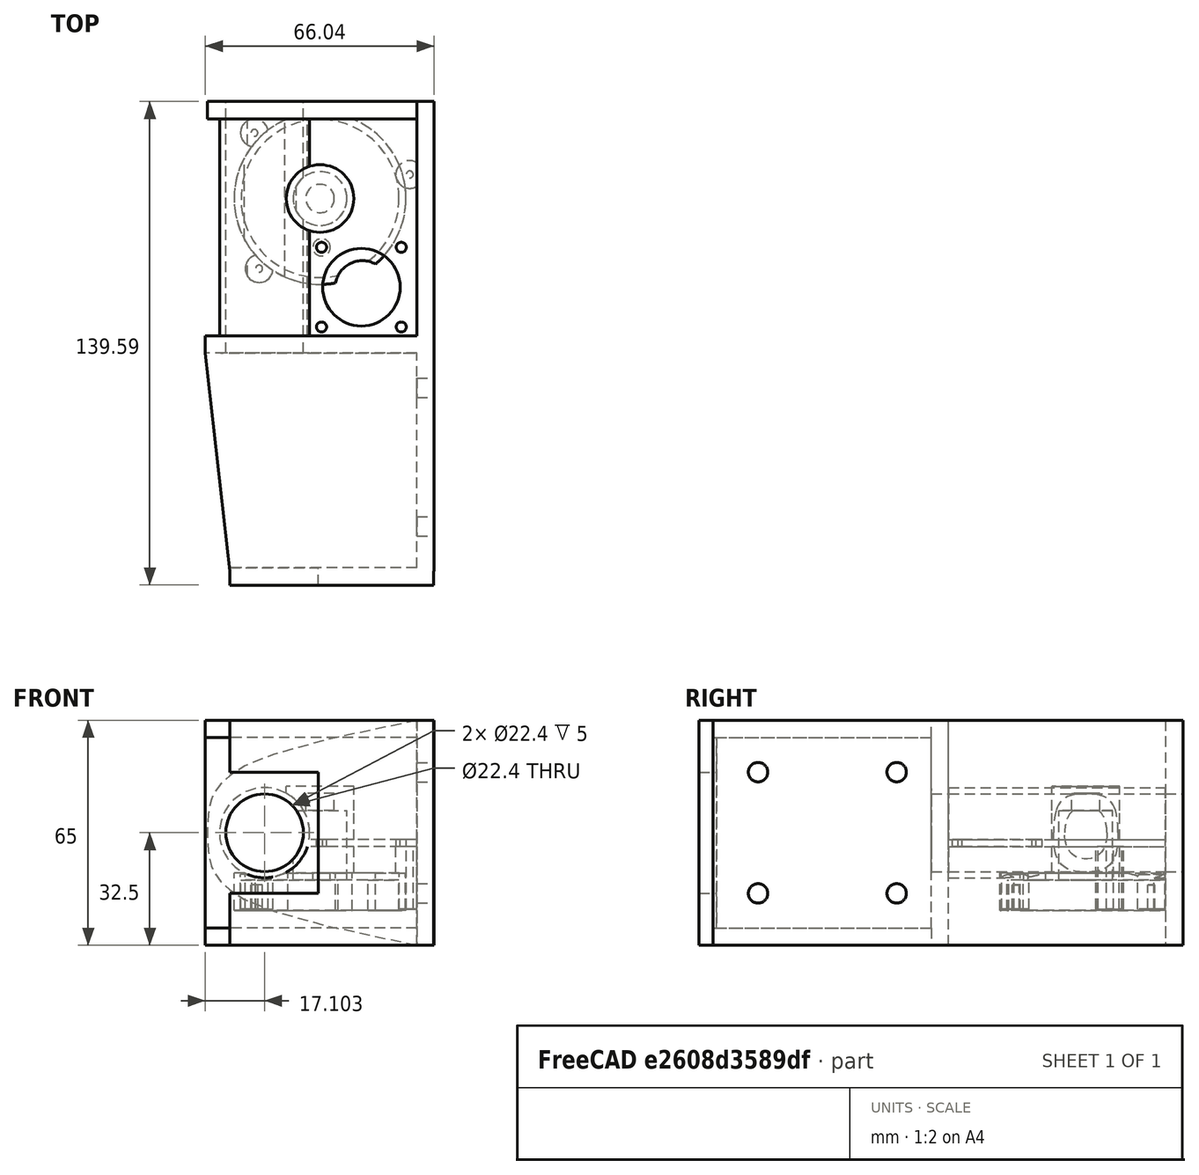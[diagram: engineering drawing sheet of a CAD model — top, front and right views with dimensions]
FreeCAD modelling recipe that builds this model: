
FCSTD DOCUMENT  (FreeCAD 0.18R16110 (Git))
Label: Thumb_Casing
License: All rights reserved
LicenseURL: http://en.wikipedia.org/wiki/All_rights_reserved
objects: Part::Cylinder×31, Part::Cut×27, Part::MultiFuse×6, Part::Box×6, Part::Wedge×2, Spreadsheet::Sheet×1, Sketcher::SketchObject×1, Part::Extrusion×1, Mesh::Feature×1
note: 74 computed .brp shape members not serialized (recipe doc carries the construction recipe); baked Part::Feature solids carry a one-line shape summary decoded from their .brp

FEATURE [Part::Cylinder] Cylinder003  label="Zylinder003"
  Angle = 360
  AttacherType = Attacher::AttachEngine3D
  Height = 72.5941
  Radius = 13
  expr: Height = Spreadsheet.z_l
  expr: Radius = Spreadsheet.z_ra + Spreadsheet.casing_srack
FEATURE [Part::Cylinder] Cylinder008  label="Zylinder008"
  Angle = 360
  AttacherType = Attacher::AttachEngine3D
  Height = 28.4
  Radius = 7.76
  expr: Height = Spreadsheet.z1_height + Spreadsheet.tolerance * 2
  expr: Radius = Spreadsheet.z1_da / 2 + Spreadsheet.tolerance * 2
FEATURE [Part::Cylinder] Cylinder004  label="Zylinder004"
  Angle = 360
  AttacherType = Attacher::AttachEngine3D
  Height = 72.5941
  Radius = 11.2
  expr: Height = Spreadsheet.z_l
  expr: Radius = Spreadsheet.z_ra + Spreadsheet.tolerance
FEATURE [Part::Cylinder] Cylinder007  label="Zylinder007"
  Angle = 360
  AttacherType = Attacher::AttachEngine3D
  Height = 8.8
  Placement = pos=(0,0,-0.4) rot=(0,0,1;0rad)
  Radius = 22.8
  expr: Placement.Base.z = -Spreadsheet.tolerance * 2
  expr: Height = Spreadsheet.z2_h + Spreadsheet.tolerance * 4
  expr: Radius = Spreadsheet.z2_da / 2 + Spreadsheet.tolerance * 2
FEATURE [Part::Cylinder] Cylinder010  label="Zylinder010"
  Angle = 360
  AttacherType = Attacher::AttachEngine3D
  Height = 5
  Radius = 4.1
FEATURE [Part::Cylinder] Cylinder006  label="Zylinder006"
  Angle = 360
  AttacherType = Attacher::AttachEngine3D
  Height = 28.4
  Radius = 9.76
  expr: Height = Spreadsheet.z1_height + Spreadsheet.tolerance * 2
  expr: Radius = Spreadsheet.z1_da / 2 + Spreadsheet.tolerance * 2 + Spreadsheet.casing_sgear
FEATURE [Part::Cylinder] Cylinder011  label="Zylinder011"
  Angle = 360
  AttacherType = Attacher::AttachEngine3D
  Height = 7
  Radius = 9.76
  expr: Height = Spreadsheet.casing_sgear + 5
  expr: Radius = Spreadsheet.z1_da / 2 + Spreadsheet.tolerance * 2 + Spreadsheet.casing_sgear
FEATURE [Part::Cylinder] Cylinder014  label="Zylinder014"
  Angle = 360
  AttacherType = Attacher::AttachEngine3D
  Height = 72.5941
  Placement = pos=(-9.44695,-21.4,12) rot=(-1,0,0;1.5708rad)
  Radius = 11.2
  expr: Placement.Base.z = Spreadsheet.z_h / 2
  expr: Height = Spreadsheet.z_l
  expr: Placement.Base.y = -(Spreadsheet.z2_da / 2 + Spreadsheet.casing_scase + Spreadsheet.casing_sgear - Spreadsheet.z1_yshift)
  expr: Placement.Base.x = -(Spreadsheet.z_ra * cos(asin(Spreadsheet.z_w / 2 / Spreadsheet.z_ra)) - Spreadsheet.modul)
  expr: Radius = Spreadsheet.z_ra + Spreadsheet.tolerance
FEATURE [Part::Cylinder] Cylinder015  label="Zylinder015"
  Angle = 360
  AttacherType = Attacher::AttachEngine3D
  Height = 10.8
  Placement = pos=(18.7793,-17.7754,-10.4) rot=(0,0,1;0rad)
  Radius = 7.84
  expr: Placement.Base.z = Spreadsheet.z2_zpos - Spreadsheet.tolerance * 2
  expr: Height = Spreadsheet.z2_h + 4 * Spreadsheet.tolerance + Spreadsheet.casing_sgear
  expr: Placement.Base.y = Spreadsheet.z1_yshift + sin(Spreadsheet.ritzel_angle) * (Spreadsheet.tolerance + Spreadsheet.z2_dc + Spreadsheet.ritzel_dc)
  expr: Placement.Base.x = Spreadsheet.z1_dc + Spreadsheet.tolerance + cos(Spreadsheet.ritzel_angle) * (Spreadsheet.tolerance + Spreadsheet.z2_dc + Spreadsheet.ritzel_dc)
  expr: Radius = Spreadsheet.ritzel_da / 2 + Spreadsheet.tolerance * 2
FEATURE [Part::Cylinder] Cylinder005  label="Zylinder005"
  Angle = 360
  AttacherType = Attacher::AttachEngine3D
  Height = 10.8
  Placement = pos=(0,0,-0.4) rot=(0,0,1;0rad)
  Radius = 24.8
  expr: Placement.Base.z = -Spreadsheet.tolerance * 2
  expr: Height = Spreadsheet.z2_h + 4 * Spreadsheet.tolerance + Spreadsheet.casing_sgear
  expr: Radius = Spreadsheet.z2_da / 2 + Spreadsheet.tolerance * 2 + Spreadsheet.casing_sgear
FEATURE [Part::MultiFuse] Fusion001
  Shapes = -> [Cylinder005,Cylinder006]
FEATURE [Part::Cylinder] Cylinder013  label="Zylinder013"
  Angle = 360
  AttacherType = Attacher::AttachEngine3D
  Height = 32.4
  Placement = pos=(6.76,8,-10.2) rot=(0,0,1;0rad)
  Radius = 9.56
  expr: Radius = Spreadsheet.z1_da / 2 + Spreadsheet.tolerance + Spreadsheet.casing_sgear
  expr: Placement.Base.y = Spreadsheet.z1_yshift
  expr: Placement.Base.x = Spreadsheet.z1_dc + Spreadsheet.tolerance
  expr: Placement.Base.z = -(Spreadsheet.z2_dr + Spreadsheet.z2_h - (Spreadsheet.z_h / 2 - Spreadsheet.z_ra) + Spreadsheet.tolerance)
  expr: Height = Spreadsheet.z_w / 2 + Spreadsheet.z2_dr + Spreadsheet.z2_h + Spreadsheet.z_ra + 2 * Spreadsheet.tolerance + Spreadsheet.casing_sgear + 4
FEATURE [Spreadsheet::Sheet] Spreadsheet
  cells = A1=Modul; B1(modul)=0.8; D1=tolerance; E1(tolerance)=0.2; G1=tolerance gear; H1(tolerance_gear)=0; A3=Zahnstange; D3=Zahnrad_1; G3=Zahnrad_2; J3=Ritzel; M3=Stepper; P3=Casing; A4=ra; B4(z_ra)=11; D4=#teeth; E4(z1_teeth)=16; G4=#teeth; H4(z2_teeth)=54; J4=#teeth; K4(ritzel_teeth)=16; M4=axis d; N4(stepper_daxis)=5; P4=gear casing sgear; Q4(casing_sgear)=2; A5=di; B5(z_ri)=8; D5=shift; E5(z1_shift)=0.2; G5=shift; H5(z2_shift)=0; J5=shift; K5(ritzel_shift)=0.3; M5=shaft l; N5(stepper_lshaft)=18; P5=rack casing srack; Q5(casing_srack)=2; A6=l; B6(z_l)==casing_ymax - casing_ymin + casing_scase; D6=pitch d; E6(z1_dpi)==modul * z1_teeth; G6=pitch d; H6(z2_dpi)==modul * z2_teeth; J6=pitch d; K6(ritzel_dpi)==modul * ritzel_teeth; M6=outside  sa; N6(stepper_sa)=28; P6=casing scase; Q6(casing_scase)=5; D7=outside d; E7(z1_da)==z1_dpi + 2 * (1 + z1_shift) * modul; G7=outside d; H7(z2_da)==z2_dpi + 2 * (1 + z2_shift) * modul; J7=outside d; K7(ritzel_da)==ritzel_dpi + 2 * (1 + ritzel_shift) * modul; M7=mount screw s; N7(stepper_sscrew)=23; P7=casing ssup; Q7(casing_ssup)=5; A8=rack height; B8(z_h)==z_th; D8=center distance; E8(z1_dc)==z1_dpi / 2 + z1_shift * modul + tolerance_gear; G8=center distance; H8(z2_dc)==z2_dpi / 2 + z2_shift * modul + tolerance_gear; J8=center distace; K8(ritzel_dc)==ritzel_dpi / 2 + ritzel_shift * modul + tolerance_gear; M8=mount d; N8(stepper_dmount)=22; P8=überlappung sjoin; Q8(casing_sjoin)=0.9; A9=rack thickness; B9(z_th)==2 * z_ra + 2; M9=mount heigth; N9(stepper_hmount)=2; A10=rack teeth width; B10(z_w)=8; D10=y Shift; E10(z1_yshift)=8; G10=height; H10(z2_h)=8; J10=angle z1; K10(ritzel_angle)=-65; M10=mount dscrew; N10(stepper_dscrew)=2.5; P10=casing y_min; Q10(casing_ymin)==-(Spreadsheet.z2_da / 2 + Spreadsheet.casing_scase + Spreadsheet.casing_sgear - Spreadsheet.z1_yshift - casing_sjoin + Spreadsheet.tolerance) * 0 + Spreadsheet.ritzel_ypos - stepper_sa / 2 - casing_scase; A11=#teeth; B11(z_teeth)=45; D11=height; E11(z1_height)==Spreadsheet.z_w * 3 / 4 + Spreadsheet.z2_dr + Spreadsheet.z2_h + Spreadsheet.z_ra; G11=distance rack; H11(z2_dr)=3; P11=casing x_min; Q11(casing_xmin)==-(Spreadsheet.z_ra * cos(asin(Spreadsheet.z_w / 2 / Spreadsheet.z_ra)) - Spreadsheet.modul + Spreadsheet.z_ra + Spreadsheet.casing_srack + Spreadsheet.casing_scase - Spreadsheet.casing_sjoin); D12=axis r; E12(z1_daxis)=2.5; G12=axis r; J12=x_pos; K12(ritzel_xpos)==Spreadsheet.z1_dc + cos(Spreadsheet.ritzel_angle) * (Spreadsheet.z2_dc + Spreadsheet.ritzel_dc); P12=casing z_min; Q12(casing_zmin)==-(Spreadsheet.z2_dr + Spreadsheet.z2_h - (Spreadsheet.z_h / 2 - Spreadsheet.z_ra) + Spreadsheet.tolerance) * 0 - 20.5; J13=y_pos; K13(ritzel_ypos)==Spreadsheet.z1_yshift + sin(Spreadsheet.ritzel_angle) * (Spreadsheet.z2_dc + Spreadsheet.ritzel_dc); G14=z_pos; H14(z2_zpos)==-(Spreadsheet.z2_dr + Spreadsheet.z2_h - (Spreadsheet.z_h / 2 - Spreadsheet.z_ra)); P14=casing z_max; Q14(casing_zmax)==(2 * Spreadsheet.casing_srack + Spreadsheet.z_th - Spreadsheet.casing_sjoin) * 0 + 44.5; G15=winkel 1; H15(z2_w1)==165°; P15=casing x_max; Q15(casing_xmax)==Spreadsheet.ritzel_xpos + stepper_sa / 2 + casing_scase + 2; A16=65; B16==-A16 / 2; C16==casing_xmax - casing_xmin - tolerance - casing_scase; G16=winkel 2; H16(z2_w2)==45°; P16=casing y_max; Q16(casing_ymax)==(Spreadsheet.ritzel_ypos + stepper_sa / 2 + 2) * 0 + 31; A17=8; B17==B16 + A18; C17==B17 ^ A20 * A19; G17=winkel 3; H17(z2_w3)==-49°; A18==A16 / A17; B18==B17 + A18; C18==B18 ^ A20 * A19; G18=winkel 4; H18(z2_w4)==-138°; A19==C16 / B16 ^ A20; B19==B18 + A18; C19==B19 ^ A20 * A19; A20=4; B20==B19 + A18; C20==B20 ^ A20 * A19; B21==B20 + A18; C21==B21 ^ A20 * A19; B22==B21 + A18; C22==B22 ^ A20 * A19; B23==B22 + A18; C23==B23 ^ A20 * A19; B24==B23 + A18; C24==B24 ^ A20 * A19
FEATURE [Part::Cut] Cut003
  Base = -> Fusion001
  Tool = -> Cylinder007
FEATURE [Part::Cut] Cut004
  Base = -> Cut003
  Placement = pos=(6.56,8,-10) rot=(0,0,1;0rad)
  Tool = -> Cylinder008
  expr: Placement.Base.z = Spreadsheet.z2_zpos
  expr: Placement.Base.y = Spreadsheet.z1_yshift
  expr: Placement.Base.x = Spreadsheet.z1_dc + Spreadsheet.tolerance_gear
FEATURE [Part::Cut] Cut002  label="casing_rack"
  Base = -> Cylinder003
  Placement = pos=(-9.44695,-36.5941,12) rot=(-1,0,0;1.5708rad)
  Tool = -> Cylinder004
  expr: Placement.Base.y = Spreadsheet.casing_ymin
  expr: Placement.Base.x = -(Spreadsheet.z_ra * cos(asin(Spreadsheet.z_w / 2 / Spreadsheet.z_ra)) - Spreadsheet.modul)
  expr: Placement.Base.z = Spreadsheet.z_h / 2
FEATURE [Part::Cut] Cut007  label="Casing_Rack"
  Base = -> Cut002
  Tool = -> Cylinder013
FEATURE [Part::Cut] Cut005
  Base = -> Cylinder011
  Placement = pos=(6.56,8,18.4) rot=(0,0,1;0rad)
  Tool = -> Cylinder010
  expr: Placement.Base.y = Spreadsheet.z1_yshift
  expr: Placement.Base.x = Spreadsheet.z1_dc + Spreadsheet.tolerance_gear
  expr: Placement.Base.z = Spreadsheet.z1_height + Spreadsheet.tolerance * 2 + Spreadsheet.z2_zpos
FEATURE [Part::MultiFuse] Fusion002
  Shapes = -> [Cut005,Cut004]
FEATURE [Part::Cut] Cut008  label="casing_übersetzung"
  Base = -> Fusion002
  Tool = -> Cylinder014
FEATURE [Part::Cut] Cut009  label="casing_übersetzung001"
  Base = -> Cut008
  Tool = -> Cylinder015
FEATURE [Part::Cylinder] Cylinder024  label="Zylinder024"
  Angle = 360
  AttacherType = Attacher::AttachEngine3D
  Height = 2
  Placement = pos=(6.76,8,0) rot=(0,0,1;0rad)
  Radius = 8.84
  expr: Placement.Base.y = Spreadsheet.z1_yshift
  expr: Placement.Base.x = Spreadsheet.z1_dc + Spreadsheet.tolerance
  expr: Height = Spreadsheet.casing_srack
  expr: Radius = Spreadsheet.z1_da / 2 + Spreadsheet.tolerance + Spreadsheet.casing_sgear - Spreadsheet.casing_sjoin * 0.8
FEATURE [Part::Cylinder] Cylinder027  label="Zylinder027"
  Angle = 360
  AttacherType = Attacher::AttachEngine3D
  Height = 2
  Placement = pos=(6.99474,-6.09413,0) rot=(0,0,1;0rad)
  Radius = 1.45
  expr: Placement.Base.y = Spreadsheet.ritzel_ypos + Spreadsheet.stepper_sscrew / 2
  expr: Placement.Base.x = Spreadsheet.ritzel_xpos - Spreadsheet.stepper_sscrew / 2
  expr: Height = Spreadsheet.casing_srack
  expr: Radius = Spreadsheet.stepper_dscrew / 2 + Spreadsheet.tolerance
FEATURE [Part::Cylinder] Cylinder030  label="Zylinder030"
  Angle = 360
  AttacherType = Attacher::AttachEngine3D
  Height = 7
  Placement = pos=(6.99474,-6.09413,-1.8) rot=(0,0,1;0rad)
  Radius = 2.5
  expr: Placement.Base.z = -(Spreadsheet.z2_dr - (Spreadsheet.z_h / 2 - Spreadsheet.z_ra) - 1 * Spreadsheet.tolerance)
  expr: Height = Spreadsheet.casing_sgear + 5
  expr: Placement.Base.y = Spreadsheet.ritzel_ypos + Spreadsheet.stepper_sscrew / 2
  expr: Placement.Base.x = Spreadsheet.ritzel_xpos - Spreadsheet.stepper_sscrew / 2
FEATURE [Part::Cut] Cut037  label="casing_übersetzung002"
  Base = -> Cut009
  Tool = -> Cylinder030
FEATURE [Part::Cylinder] Cylinder025  label="Zylinder025"
  Angle = 360
  AttacherType = Attacher::AttachEngine3D
  Height = 2
  Placement = pos=(18.4947,-17.5941,0) rot=(0,0,1;0rad)
  Radius = 11.2
  expr: Placement.Base.y = Spreadsheet.ritzel_ypos
  expr: Placement.Base.x = Spreadsheet.ritzel_xpos
  expr: Radius = Spreadsheet.stepper_dmount / 2 + Spreadsheet.tolerance
  expr: Height = Spreadsheet.casing_srack
FEATURE [Part::Box] Box006  label="Quader002"
  AttacherType = Attacher::AttachEngine3D
  Height = 2
  Length = 36.6417
  Placement = pos=(2.85305,-36.5941,0) rot=(0,0,1;0rad)
  Width = 72.5941
  expr: Length = Spreadsheet.casing_xmax - (-(Spreadsheet.z_ra * cos(asin(Spreadsheet.z_w / 2 / Spreadsheet.z_ra)) - Spreadsheet.modul) + Spreadsheet.z_ra + Spreadsheet.tolerance + Spreadsheet.casing_srack - Spreadsheet.casing_sjoin)
  expr: Placement.Base.y = Spreadsheet.casing_ymin
  expr: Placement.Base.x = -(Spreadsheet.z_ra * cos(asin(Spreadsheet.z_w / 2 / Spreadsheet.z_ra)) - Spreadsheet.modul) + Spreadsheet.z_ra + Spreadsheet.tolerance + Spreadsheet.casing_srack - Spreadsheet.casing_sjoin
  expr: Width = Spreadsheet.z_l
  expr: Height = Spreadsheet.casing_srack
FEATURE [Part::Cut] Cut017
  Base = -> Box006
  Tool = -> Cylinder024
FEATURE [Part::Cut] Cut018
  Base = -> Cut017
  Tool = -> Cylinder025
FEATURE [Part::Cylinder] Cylinder028  label="Zylinder028"
  Angle = 360
  AttacherType = Attacher::AttachEngine3D
  Height = 2
  Placement = pos=(6.99474,-29.0941,0) rot=(0,0,1;0rad)
  Radius = 1.45
  expr: Placement.Base.y = Spreadsheet.ritzel_ypos - Spreadsheet.stepper_sscrew / 2
  expr: Placement.Base.x = Spreadsheet.ritzel_xpos - Spreadsheet.stepper_sscrew / 2
  expr: Height = Spreadsheet.casing_srack
  expr: Radius = Spreadsheet.stepper_dscrew / 2 + Spreadsheet.tolerance
FEATURE [Part::Cylinder] Cylinder029  label="Zylinder029"
  Angle = 360
  AttacherType = Attacher::AttachEngine3D
  Height = 2
  Placement = pos=(29.9947,-29.0941,0) rot=(0,0,1;0rad)
  Radius = 1.45
  expr: Placement.Base.y = Spreadsheet.ritzel_ypos - Spreadsheet.stepper_sscrew / 2
  expr: Placement.Base.x = Spreadsheet.ritzel_xpos + Spreadsheet.stepper_sscrew / 2
  expr: Height = Spreadsheet.casing_srack
  expr: Radius = Spreadsheet.stepper_dscrew / 2 + Spreadsheet.tolerance
FEATURE [Part::Cylinder] Cylinder026  label="Zylinder026"
  Angle = 360
  AttacherType = Attacher::AttachEngine3D
  Height = 2
  Placement = pos=(29.9947,-6.09413,0) rot=(0,0,1;0rad)
  Radius = 1.45
  expr: Placement.Base.y = Spreadsheet.ritzel_ypos + Spreadsheet.stepper_sscrew / 2
  expr: Placement.Base.x = Spreadsheet.ritzel_xpos + Spreadsheet.stepper_sscrew / 2
  expr: Height = Spreadsheet.casing_srack
  expr: Radius = Spreadsheet.stepper_dscrew / 2 + Spreadsheet.tolerance
FEATURE [Part::Cut] Cut019
  Base = -> Cut018
  Tool = -> Cylinder026
FEATURE [Part::Cut] Cut020
  Base = -> Cut019
  Tool = -> Cylinder027
FEATURE [Part::Cut] Cut021
  Base = -> Cut020
  Tool = -> Cylinder028
FEATURE [Part::Cut] Cut022  label="Mount_Plate"
  Base = -> Cut021
  Placement = pos=(0,0,8) rot=(0,0,1;0rad)
  Tool = -> Cylinder029
  expr: Placement.Base.z = -(Spreadsheet.z2_dr + Spreadsheet.z2_h - (Spreadsheet.z_h / 2 - Spreadsheet.z_ra)) + Spreadsheet.stepper_lshaft + Spreadsheet.stepper_hmount - Spreadsheet.casing_srack
FEATURE [Part::Cylinder] Cylinder119  label="Zylinder119"
  Angle = 360
  AttacherType = Attacher::AttachEngine3D
  Height = 10
  Placement = pos=(6.56,8,-10) rot=(0,0,1;0rad)
  Radius = 24.8
  expr: Placement.Base.z = Spreadsheet.z2_zpos
  expr: Placement.Base.y = Spreadsheet.z1_yshift
  expr: Placement.Base.x = Spreadsheet.z1_dc + Spreadsheet.tolerance_gear
  expr: Radius = Spreadsheet.z2_da / 2 + Spreadsheet.tolerance * 2 + Spreadsheet.casing_sgear
FEATURE [Part::Cylinder] Cylinder122  label="Zylinder122"
  Angle = 360
  AttacherType = Attacher::AttachEngine3D
  Height = 19
  Radius = 4
FEATURE [Part::Cylinder] Cylinder117  label="Zylinder117"
  Angle = 360
  AttacherType = Attacher::AttachEngine3D
  Height = 7
  Radius = 1
FEATURE [Part::Cylinder] Cylinder120  label="Zylinder120"
  Angle = 360
  AttacherType = Attacher::AttachEngine3D
  Height = 10
  Placement = pos=(6.56,8,-10) rot=(0,0,1;0rad)
  Radius = 24.8
  expr: Placement.Base.z = Spreadsheet.z2_zpos
  expr: Placement.Base.y = Spreadsheet.z1_yshift
  expr: Placement.Base.x = Spreadsheet.z1_dc + Spreadsheet.tolerance_gear
  expr: Radius = Spreadsheet.z2_da / 2 + Spreadsheet.tolerance * 2 + Spreadsheet.casing_sgear
FEATURE [Part::Cylinder] Cylinder116  label="Zylinder116"
  Angle = 360
  AttacherType = Attacher::AttachEngine3D
  Height = 10
  Radius = 4
FEATURE [Part::Cut] Cut084
  Base = -> Cylinder116
  Placement = pos=(-12.3905,26.9505,-10) rot=(0,0,1;0rad)
  Tool = -> Cylinder117
  expr: Placement.Base.z = Spreadsheet.z2_zpos
  expr: Placement.Base.y = Spreadsheet.z1_yshift + (Spreadsheet.z2_da / 2 + Spreadsheet.tolerance * 2 + Spreadsheet.casing_sgear + 2) * sin(Spreadsheet.z2_w2)
  expr: Placement.Base.x = Spreadsheet.z1_dc + Spreadsheet.tolerance_gear - (Spreadsheet.z2_da / 2 + Spreadsheet.tolerance * 2 + Spreadsheet.casing_sgear + 2) * cos(Spreadsheet.z2_w2)
FEATURE [Part::Cut] Cut088  label="Befestigung2"
  Base = -> Cut084
  Tool = -> Cylinder119
FEATURE [Part::Cut] Cut086
  Base = -> Cylinder116
  Placement = pos=(-11.0224,-12.2262,-10) rot=(0,0,1;0rad)
  Tool = -> Cylinder117
  expr: Placement.Base.z = Spreadsheet.z2_zpos
  expr: Placement.Base.y = Spreadsheet.z1_yshift + (Spreadsheet.z2_da / 2 + Spreadsheet.tolerance * 2 + Spreadsheet.casing_sgear + 2) * sin(Spreadsheet.z2_w3)
  expr: Placement.Base.x = Spreadsheet.z1_dc + Spreadsheet.tolerance_gear - (Spreadsheet.z2_da / 2 + Spreadsheet.tolerance * 2 + Spreadsheet.casing_sgear + 2) * cos(Spreadsheet.z2_w3)
FEATURE [Part::Cut] Cut089  label="Befestigung3"
  Base = -> Cut086
  Tool = -> Cylinder120
FEATURE [Part::MultiFuse] Fusion047
  Shapes = -> [Cut037,Cut088]
FEATURE [Part::MultiFuse] Fusion048
  Shapes = -> [Fusion047,Cut089]
FEATURE [Part::Cylinder] Cylinder123  label="Zylinder123"
  Angle = 360
  AttacherType = Attacher::AttachEngine3D
  Height = 19
  Radius = 1
FEATURE [Part::Cut] Cut091
  Base = -> Cylinder122
  Placement = pos=(32.4468,14.9364,-10) rot=(0,0,1;0rad)
  Tool = -> Cylinder123
  expr: Placement.Base.z = Spreadsheet.z2_zpos
  expr: Placement.Base.y = Spreadsheet.z1_yshift + (Spreadsheet.z2_da / 2 + Spreadsheet.tolerance * 2 + Spreadsheet.casing_sgear + 2) * sin(Spreadsheet.z2_w1)
  expr: Placement.Base.x = Spreadsheet.z1_dc + Spreadsheet.tolerance_gear - (Spreadsheet.z2_da / 2 + Spreadsheet.tolerance * 2 + Spreadsheet.casing_sgear + 2) * cos(Spreadsheet.z2_w1)
FEATURE [Part::Box] Box016  label="Quader011"
  AttacherType = Attacher::AttachEngine3D
  Height = 65
  Length = 58.8
  Placement = pos=(-14.447,-83.5941,-20.5) rot=(0,0,1;0rad)
  Width = 5
  expr: Placement.Base.z = Spreadsheet.z_h / 2 - 65 / 2
  expr: Placement.Base.y = Spreadsheet.casing_ymin - 37 - 10
  expr: Placement.Base.x = -(Spreadsheet.z_ra * cos(asin(Spreadsheet.z_w / 2 / Spreadsheet.z_ra)) - Spreadsheet.modul) - 5
FEATURE [Part::Cylinder] Cylinder124  label="Zylinder124"
  Angle = 360
  AttacherType = Attacher::AttachEngine3D
  Height = 10
  Placement = pos=(6.56,8,-10) rot=(0,0,1;0rad)
  Radius = 24.8
  expr: Placement.Base.z = Spreadsheet.z2_zpos
  expr: Placement.Base.y = Spreadsheet.z1_yshift
  expr: Placement.Base.x = Spreadsheet.z1_dc + Spreadsheet.tolerance_gear
  expr: Radius = Spreadsheet.z2_da / 2 + Spreadsheet.tolerance * 2 + Spreadsheet.casing_sgear
FEATURE [Part::Cut] Cut092  label="Befestigung1"
  Base = -> Cut091
  Tool = -> Cylinder124
FEATURE [Part::MultiFuse] Fusion049  label="Casing_Gear"
  Shapes = -> [Fusion048,Cut092]
FEATURE [Part::Cylinder] Cylinder129  label="Zylinder129"
  Angle = 360
  AttacherType = Attacher::AttachEngine3D
  Height = 5
  Placement = pos=(-9.44695,31,12) rot=(-1,0,0;1.5708rad)
  Radius = 11.2
  expr: Placement.Base.y = 36 - Spreadsheet.casing_scase
  expr: Placement.Base.x = -(Spreadsheet.z_ra * cos(asin(Spreadsheet.z_w / 2 / Spreadsheet.z_ra)) - Spreadsheet.modul)
  expr: Placement.Base.z = Spreadsheet.z_h / 2
  expr: Height = Spreadsheet.casing_scase
  expr: Radius = Spreadsheet.z_ra + Spreadsheet.tolerance
FEATURE [Part::Box] Box022  label="Quader016"
  AttacherType = Attacher::AttachEngine3D
  Height = 35
  Length = 25.5
  Placement = pos=(-14.447,-83.5941,-5.5) rot=(0,0,1;0rad)
  Width = 5
  expr: Placement.Base.z = Spreadsheet.z_h / 2 - 35 / 2
  expr: Placement.Base.y = Spreadsheet.casing_ymin - 37 - 10
  expr: Placement.Base.x = -(Spreadsheet.z_ra * cos(asin(Spreadsheet.z_w / 2 / Spreadsheet.z_ra)) - Spreadsheet.modul) - 5
  expr: Width = Spreadsheet.casing_scase
FEATURE [Part::Cut] Cut106  label="Bottom_I"
  Base = -> Box016
  Placement = pos=(-5,-20,0) rot=(0,0,1;0rad)
  Tool = -> Box022
FEATURE [Sketcher::SketchObject] Sketch
  Placement = pos=(0,0,0) rot=(1,0,0;1.5708rad)
  expr: Constraints[17] = Spreadsheet.C24
  expr: Constraints[9] = Spreadsheet.C20
  expr: Constraints[14] = Spreadsheet.B23
  expr: Constraints[15] = Spreadsheet.C23
  expr: Constraints[13] = Spreadsheet.C22
  expr: Constraints[7] = Spreadsheet.C19
  expr: Constraints[11] = Spreadsheet.C21
  expr: Constraints[8] = Spreadsheet.B20
  expr: Constraints[16] = Spreadsheet.B24
  expr: Constraints[1] = Spreadsheet.C16
  expr: Constraints[12] = Spreadsheet.B22
  expr: Constraints[5] = Spreadsheet.C18
  expr: Constraints[2] = Spreadsheet.B17
  expr: Constraints[10] = Spreadsheet.B21
  expr: Constraints[4] = Spreadsheet.B18
  expr: Constraints[3] = Spreadsheet.C17
  expr: Constraints[6] = Spreadsheet.B19
  expr: Constraints[0] = Spreadsheet.B16
  sketch-geometry (44):
    g0: GeomPoint X=-32.5 Y=60.8417 Z=0
    g1: GeomPoint X=-16.25 Y=3.80261 Z=0
    g2: GeomPoint X=0 Y=0 Z=0
    g3: GeomPoint X=8.125 Y=0.237663 Z=0
    g4: GeomPoint X=16.25 Y=3.80261 Z=0
    g5: GeomPoint X=24.375 Y=19.2507 Z=0
    g6: GeomPoint X=-24.375 Y=19.2507 Z=0
    g7: GeomPoint X=-8.125 Y=0.237663 Z=0
    g8: GeomPoint X=32.5 Y=60.8417 Z=0
    g9: Circle [constr] CenterX=-32.5 CenterY=60.8417 CenterZ=0 NormalX=0 NormalY=0 NormalZ=1 AngleXU=0 Radius=6
    g10: Circle [constr] CenterX=-24.375 CenterY=19.2507 CenterZ=0 NormalX=0 NormalY=0 NormalZ=1 AngleXU=0 Radius=6
    g11: Circle [constr] CenterX=-16.25 CenterY=3.80261 CenterZ=0 NormalX=0 NormalY=0 NormalZ=1 AngleXU=0 Radius=6
    g12: Circle [constr] CenterX=0 CenterY=0 CenterZ=0 NormalX=0 NormalY=0 NormalZ=1 AngleXU=0 Radius=6
    g13: Circle [constr] CenterX=8.125 CenterY=0.237663 CenterZ=0 NormalX=0 NormalY=0 NormalZ=1 AngleXU=0 Radius=6
    g14: Circle [constr] CenterX=16.25 CenterY=3.80261 CenterZ=0 NormalX=0 NormalY=0 NormalZ=1 AngleXU=0 Radius=6
    g15: Circle [constr] CenterX=24.375 CenterY=19.2507 CenterZ=0 NormalX=0 NormalY=0 NormalZ=1 AngleXU=0 Radius=6
    g16: Circle [constr] CenterX=32.5 CenterY=60.8417 CenterZ=0 NormalX=0 NormalY=0 NormalZ=1 AngleXU=0 Radius=6
    g17: Circle [constr] CenterX=-32.5 CenterY=60.8417 CenterZ=0 NormalX=0 NormalY=0 NormalZ=1 AngleXU=0 Radius=6
    g18: Circle [constr] CenterX=-24.375 CenterY=19.2507 CenterZ=0 NormalX=0 NormalY=0 NormalZ=1 AngleXU=0 Radius=6
    g19: Circle [constr] CenterX=-16.25 CenterY=3.80261 CenterZ=0 NormalX=0 NormalY=0 NormalZ=1 AngleXU=0 Radius=6
    g20: Circle [constr] CenterX=-8.125 CenterY=0.237663 CenterZ=0 NormalX=0 NormalY=0 NormalZ=1 AngleXU=0 Radius=6
    g21: Circle [constr] CenterX=0 CenterY=0 CenterZ=0 NormalX=0 NormalY=0 NormalZ=1 AngleXU=0 Radius=6
    g22: Circle [constr] CenterX=8.125 CenterY=0.237663 CenterZ=0 NormalX=0 NormalY=0 NormalZ=1 AngleXU=0 Radius=6
    g23: Circle [constr] CenterX=16.25 CenterY=3.80261 CenterZ=0 NormalX=0 NormalY=0 NormalZ=1 AngleXU=0 Radius=6
    g24: Circle [constr] CenterX=24.375 CenterY=19.2507 CenterZ=0 NormalX=0 NormalY=0 NormalZ=1 AngleXU=0 Radius=6
    g25: Circle [constr] CenterX=32.5 CenterY=60.8417 CenterZ=0 NormalX=0 NormalY=0 NormalZ=1 AngleXU=0 Radius=6
    g26: LineSegment StartX=-32.5 StartY=60.8417 StartZ=0 EndX=32.5 EndY=60.8417 EndZ=0
    g27-g35: Circle [constr] x9 (B-spline internal-alignment scaffolding for g36; pole/knot coordinates omitted)
    g36: BSplineCurve PolesCount=9 KnotsCount=7 Degree=3 IsPeriodic=0
    g37-g43: GeomPoint [constr] x7 (B-spline internal-alignment scaffolding for g36; pole/knot coordinates omitted)
  constraints (74):
    c: DistanceX(g0) = -32.5
    c: DistanceY(g0) = 60.8417
    c: DistanceX(g6) = -24.375
    c: DistanceY(g6) = 19.2507
    c: DistanceX(g1) = -16.25
    c: DistanceY(g1) = 3.80261
    c: DistanceX(g7) = -8.125
    c: DistanceY(g7) = 0.237663
    c: DistanceX(g2) = 0
    c: DistanceY(g2) = 0
    c: DistanceX(g3) = 8.125
    c: DistanceY(g3) = 0.237663
    c: DistanceX(g4) = 16.25
    c: DistanceY(g4) = 3.80261
    c: DistanceX(g5) = 24.375
    c: DistanceY(g5) = 19.2507
    c: DistanceX(g8) = 32.5
    c: DistanceY(g8) = 60.8417
    c: Coincident(g9,g0)
    c: Radius(g9) = 6
    c: Equal(g9,g10)
    c: Coincident(g10,g6)
    c: Equal(g9,g11)
    c: Coincident(g11,g1)
    c: Equal(g9,g12)
    c: Coincident(g12,g-1)
    c: Equal(g9,g13)
    c: Coincident(g13,g3)
    c: Equal(g9,g14)
    c: Coincident(g14,g4)
    c: Equal(g9,g15)
    c: Coincident(g15,g5)
    c: Equal(g9,g16)
    c: Coincident(g16,g8)
    c: Coincident(g17,g0)
    c: Radius(g17) = 6
    c: Equal(g17,g18)
    c: Coincident(g18,g6)
    c: Equal(g17,g19)
    c: Coincident(g19,g1)
    c: Equal(g17,g20)
    c: Coincident(g20,g7)
    c: Equal(g17,g21)
    c: Coincident(g21,g-1)
    c: Equal(g17,g22)
    c: Coincident(g22,g3)
    c: Equal(g17,g23)
    c: Coincident(g23,g4)
    c: Equal(g17,g24)
    c: Coincident(g24,g5)
    c: Equal(g17,g25)
    c: Coincident(g25,g8)
    c: Coincident(g26,g0)
    c: Coincident(g26,g8)
    c: Coincident(g27,g0)
    c: Radius(g27) = 6
    c: Equal(g27,g28)
    c: Coincident(g28,g6)
    c: Equal(g27,g29)
    c: Coincident(g29,g1)
    c: Equal(g27,g30)
    c: Coincident(g30,g7)
    c: Equal(g27,g31)
    c: Coincident(g31,g-1)
    c: Equal(g27,g32)
    c: Coincident(g32,g3)
    c: Equal(g27,g33)
    c: Coincident(g33,g4)
    c: Equal(g27,g34)
    c: Coincident(g34,g5)
    c: Equal(g27,g35)
    c: Coincident(g35,g8)
    c: InternalAlignment(g27-g35 -> g36) x9
    c: InternalAlignment(g37-g43 -> g36) x7
FEATURE [Part::Extrusion] Extrude001  label="Top"
  Base = -> Sketch
  Dir = (0,-1,0)
  DirMode = 2
  FaceMakerClass = Part::FaceMakerBullseye
  LengthFwd = 5
  LengthRev = 0
  Placement = pos=(-26,36,12) rot=(0,1,0;1.5708rad)
  Solid = true
  Symmetric = false
FEATURE [Part::Cut] Cut099  label="Top001"
  Base = -> Extrude001
  Tool = -> Cylinder129
FEATURE [Part::Cylinder] Cylinder131  label="Zylinder131"
  Angle = 360
  AttacherType = Attacher::AttachEngine3D
  Height = 5
  Placement = pos=(34.4947,-46.5941,29.5) rot=(0,1,0;1.5708rad)
  Radius = 2.8
  expr: Placement.Base.z = Spreadsheet006.casing_zmax - 10 - Spreadsheet.casing_ssup
  expr: Height = Spreadsheet006.casing_ssup
  expr: Placement.Base.y = Spreadsheet006.casing_ymin - 10
  expr: Placement.Base.x = Spreadsheet006.casing_xmax - Spreadsheet.casing_ssup
  expr: Radius = Spreadsheet006.tolerance + 5.2 / 2
FEATURE [Part::Cylinder] Cylinder130  label="Zylinder130"
  Angle = 360
  AttacherType = Attacher::AttachEngine3D
  Height = 5
  Placement = pos=(34.4947,-46.5941,-5.5) rot=(0,1,0;1.5708rad)
  Radius = 2.8
  expr: Placement.Base.z = Spreadsheet006.casing_zmin + 10 + Spreadsheet.casing_ssup
  expr: Height = Spreadsheet006.casing_ssup
  expr: Placement.Base.y = Spreadsheet006.casing_ymin - 10
  expr: Placement.Base.x = Spreadsheet006.casing_xmax - Spreadsheet.casing_ssup
  expr: Radius = Spreadsheet006.tolerance + 5.2 / 2
FEATURE [Part::Box] Box023  label="Quader017"
  AttacherType = Attacher::AttachEngine3D
  Height = 65
  Length = 5
  Placement = pos=(34.4947,-99.5941,-20.5) rot=(0,0,1;0rad)
  Width = 63
  expr: Placement.Base.x = Spreadsheet006.casing_xmax - Spreadsheet.casing_ssup
  expr: Placement.Base.y = Spreadsheet006.casing_ymin - Spreadsheet.casing_ssup - 58
  expr: Placement.Base.z = Spreadsheet006.casing_zmin
FEATURE [Part::Cut] Cut111
  Base = -> Box023
  Tool = -> Cylinder130
FEATURE [Part::Box] Box025  label="Boden004"
  AttacherType = Attacher::AttachEngine3D
  Height = 65
  Length = 66.0417
  Placement = pos=(-26.547,0,-20.5) rot=(0,0,1;0rad)
  Width = 5
  expr: Width = Spreadsheet010.casing_scase
  expr: Length = Spreadsheet010.casing_xmax - Spreadsheet.casing_xmin
  expr: Placement.Base.z = Spreadsheet010.casing_zmin
  expr: Height = Spreadsheet010.casing_zmax - Spreadsheet.casing_zmin
  expr: Placement.Base.x = Spreadsheet010.casing_xmin
FEATURE [Part::Cylinder] Cylinder133  label="Zylinder133"
  Angle = 360
  AttacherType = Attacher::AttachEngine3D
  Height = 5
  Placement = pos=(34.4947,-86.5941,-5.5) rot=(0,1,0;1.5708rad)
  Radius = 2.8
  expr: Placement.Base.z = Spreadsheet006.casing_zmin + 10 + Spreadsheet.casing_ssup
  expr: Height = Spreadsheet006.casing_ssup
  expr: Placement.Base.y = Spreadsheet006.casing_ymin + 10 - 60
  expr: Placement.Base.x = Spreadsheet006.casing_xmax - Spreadsheet.casing_ssup
  expr: Radius = Spreadsheet006.tolerance + 5.2 / 2
FEATURE [Part::Cylinder] Cylinder132  label="Zylinder132"
  Angle = 360
  AttacherType = Attacher::AttachEngine3D
  Height = 5
  Placement = pos=(34.4947,-86.5941,29.5) rot=(0,1,0;1.5708rad)
  Radius = 2.8
  expr: Placement.Base.z = Spreadsheet006.casing_zmax - 10 - Spreadsheet.casing_ssup
  expr: Height = Spreadsheet006.casing_ssup
  expr: Placement.Base.y = Spreadsheet006.casing_ymin + 10 - 60
  expr: Placement.Base.x = Spreadsheet006.casing_xmax - Spreadsheet.casing_ssup
  expr: Radius = Spreadsheet006.tolerance + 5.2 / 2
FEATURE [Part::Cut] Cut113
  Base = -> Cut111
  Tool = -> Cylinder132
FEATURE [Part::Cut] Cut114
  Base = -> Cut113
  Tool = -> Cylinder131
FEATURE [Part::Cut] Cut112  label="Back_II"
  Base = -> Cut114
  Tool = -> Cylinder133
FEATURE [Part::Cylinder] Cylinder134  label="Zylinder134"
  Angle = 360
  AttacherType = Attacher::AttachEngine3D
  Height = 5
  Placement = pos=(-9.44695,0,12) rot=(-1,0,0;1.5708rad)
  Radius = 11.2
  expr: Placement.Base.z = Spreadsheet010.z_h / 2
  expr: Height = Spreadsheet010.casing_scase
  expr: Placement.Base.x = -(Spreadsheet.z_ra * cos(asin(Spreadsheet.z_w / 2 / Spreadsheet.z_ra)) - Spreadsheet.modul)
  expr: Radius = Spreadsheet010.z_ra + Spreadsheet.tolerance
FEATURE [Part::Cut] Cut115  label="Bottom_I001"
  Base = -> Box025
  Placement = pos=(0,-36.5941,0) rot=(0,0,1;0rad)
  Tool = -> Cylinder134
  expr: Placement.Base.y = Spreadsheet010.casing_ymin
FEATURE [Part::Box] Box024  label="Back_I"
  AttacherType = Attacher::AttachEngine3D
  Height = 65
  Length = 5
  Placement = pos=(34.4947,-36.5941,-20.5) rot=(0,0,1;0rad)
  Width = 72.5941
  expr: Length = Spreadsheet009.casing_scase
  expr: Width = Spreadsheet009.z_l
  expr: Placement.Base.y = Spreadsheet009.casing_ymin
  expr: Placement.Base.x = Spreadsheet009.casing_xmax - Spreadsheet.casing_scase
  expr: Placement.Base.z = Spreadsheet009.casing_zmin
  expr: Height = -Spreadsheet.casing_zmin + Spreadsheet.casing_zmax
FEATURE [Part::Wedge] Wedge003  label="Side_II"
  AttacherType = Attacher::AttachEngine3D
  Placement = pos=(39.4947,-99.5941,44.5) rot=(0,1,0;3.14159rad)
  X2max = 66.0417
  X2min = 0
  Xmax = 58.9417
  Xmin = 0
  Ymax = 63
  Ymin = 0
  Z2max = 5
  Z2min = 0
  Zmax = 5
  Zmin = 0
  expr: Placement.Base.y = Spreadsheet008.casing_ymin - 63
  expr: Placement.Base.x = Spreadsheet008.casing_xmax
  expr: Placement.Base.z = Spreadsheet008.casing_zmax
  expr: X2max = Spreadsheet008.casing_xmax - Spreadsheet.casing_xmin
  expr: Xmax = 10 + Spreadsheet.casing_xmax + Spreadsheet.z_ra * cos(asin(Spreadsheet.z_w / 2 / Spreadsheet.z_ra)) - Spreadsheet.modul
  expr: Zmax = Spreadsheet008.casing_scase
  expr: Z2max = Spreadsheet008.casing_scase
FEATURE [Part::Wedge] Wedge002  label="Side_I"
  AttacherType = Attacher::AttachEngine3D
  Placement = pos=(39.4947,-99.5941,-15.5) rot=(0,1,0;3.14159rad)
  X2max = 66.0417
  X2min = 0
  Xmax = 58.9417
  Xmin = 0
  Ymax = 63
  Ymin = 0
  Z2max = 5
  Z2min = 0
  Zmax = 5
  Zmin = 0
  expr: Placement.Base.y = Spreadsheet007.casing_ymin - 63
  expr: Placement.Base.x = Spreadsheet007.casing_xmax
  expr: Placement.Base.z = Spreadsheet007.casing_zmin + Spreadsheet.casing_scase
  expr: X2max = Spreadsheet007.casing_xmax - Spreadsheet.casing_xmin
  expr: Xmax = Spreadsheet007.casing_xmax + Spreadsheet.z_ra * cos(asin(Spreadsheet.z_w / 2 / Spreadsheet.z_ra)) - Spreadsheet.modul + 10
  expr: Zmax = Spreadsheet007.casing_scase
  expr: Z2max = Spreadsheet007.casing_scase
FEATURE [Part::MultiFuse] Fusion055  label="Thumb_Casing"
  Shapes = -> [Cut007,Cut022,Cut099,Fusion049,Cut106,Cut112,Wedge002,Box024,Cut115,Wedge003]
FEATURE [Mesh::Feature] Mesh  label="Thumb_Casing (Meshed)"
